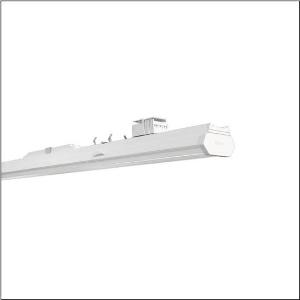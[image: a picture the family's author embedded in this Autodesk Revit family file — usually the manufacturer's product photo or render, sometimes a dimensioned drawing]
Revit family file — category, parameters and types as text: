
# Revit family: licross_r__11_protected_ho_51tp12mn4f5m_a747
name_source: partatom
category: Lighting Fixtures
units: mm (PartAtom-declared; Revit-internal decimal feet)

## family parameters
Cut with Voids When Loaded = No
Host = Face
Light Source = No
Part Type = Normal
Room Calculation Point = No
Round Connector Dimension = Use Diameter
Shared = No

## types (1)
- --- (1 x LED, 15820 lm, 87.4 W, 4000K)
    Apparent Load = 87 VA
    CIE Flux Codes = 70 91 97 98 100
    Color Rendering = 80
    Color Temperature = 4000K
    Default Elevation = 1800 mm
    Description = Licross® 11 Protected HO, luminaire insert, of sheet steel, galvanised, coil coated, white, length: 1.500mm, width: 90mm, height: 101mm, LED rated luminous flux: 15.820lm, light colour: 840, control gear: ON/OFF Multilumen, with plug, 3-pole, with phase selection, mains connection: 220..240V, AC, 50/60Hz, rated input power: 87W, halogen-free wiring, primary light control with lens, of plastic, primary optical cover: cover, of PMMA, light emission: direct distribution, primary light characteristic: symmetric, protection rating (complete): IP64, insulation class (complete): insulation class I (protective earthing), certification: CE, ENEC, VDE, UKCA, protection symbol: D if used in an environment with conductive dust loads with corresponding accessories, impact resistance: IK06, permissible ambient temperature for indoor applications: -35..+35°C, corresponds to IFS (International Featured Standards) requirements for safety and quality in the food industry, reducing of maximum allowable ambient temperature of 5°C with ceiling mounting, LABS conformity tested according to VDMA 24364:2018-05, packaging unit: 1 piece
    Height = 92 mm
    Lamp = 1 x LED
    Lamp Light Flux = 15820 lm
    Lamp Power = 87.4 W
    Lamp count = 1
    Length = 1500 mm
    Luminous efficacy = 181 lm/W
    Manufacturer = Siteco
    ModVariant = No
    Model = 51TP12MN4F5M
    Mounting Place = Ceiling
    Mounting Type = Pendant
    Number of Poles = 1
    OnlyDefault = Yes
    Power Factor = 1
    Product Name = Licross® 11 Protected HO
    Product group = luminaire insert
    ProductGroupID = 901
    Protection Class = Protection class I
    Protection Degree = IP 64
    RLX_Detail_Level = 1
    RLX_Emergency_Light_Flux = 0 lm
    RLX_Emergency_Type = 0
    RLX_Emergency_Type_DB = No
    RlxData = <blob elided: 22093 chars, md5=1def94b7>
    Socket = socket
    Standby Power = 0 W
    System Light Flux = 15820 lm
    System Power = 87 W
    Type Comments = factory setting: luminous flux: 100 % | (A | C | E) | 203 mA
    Type Image = l_1256148.jpg
    URL = http://relux.com
    VarID = @adj_019495
    Voltage = 0 V
    Weight = 0.00 kg
    Width = 88 mm

## geometry (parser evidence)
native form markers: Blend x4, Sweep x9
no freeform markers — native parametric forms only
